# Revit family: Скамейка стальная «Wood Bench» с USB-входами Арт 20364
name_source: partatom
category: Антураж
revit_build: Autodesk Revit 2018 (Build: 20180423_1000(x64)
units: mm (PartAtom-declared; Revit-internal decimal feet)

## family parameters
Всегда вертикально = Да
Источник визуального образа = Геометрия семейства
На основе рабочей плоскости = Нет
Общий = Нет
При загрузке вырезать с полостями = Нет
Точка расчета площади = Нет

## types (2) — shared parameters
Артикул товара = Арт. 20364
Высота = 700 мм
Группа модели = Скамейки
Изготовитель = ООО «Хоббика»
Материал изделия = Сталь, дерево
Цвет лавки = Дерево
Цвет опоры = Сталь
Ширина = 500 мм

## per-type parameters (varying)
| type | Версия 2,0 м | Версия 3,0 м | Длина | Изображение типоразмера | Описание |
| Версия 2,0 м | Да | Нет | 2000 мм | Скамейка стальная «Wood Bench» с USB-входами Арт 20364 2,0 м.jpg | Скамейка стальная «Wood Bench» с USB-входами. Версия 2,0 м с одной спинкой |
| Версия 3,0 м | Нет | Да | 3000 мм | Скамейка стальная «Wood Bench» с USB-входами Арт 20364 3,0 м.jpg | Скамейка стальная «Wood Bench» с USB-входами. Версия 3,0 м с двумя спинками |
